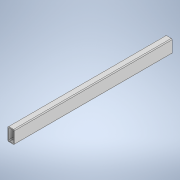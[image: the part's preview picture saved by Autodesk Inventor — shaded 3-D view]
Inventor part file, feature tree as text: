
AUTODESK INVENTOR PART (.ipt)
format: ipt  version: 2020 (Build 240168000, 168)  size: 124,416 bytes
history: native  units: in
note: dims shown in document units (in); Inventor stores cm internally (conversion verified against a paired STEP export)
features: extrude x1, sketch x1
ambient origin geometry x8: Origin, YZ Plane, XZ Plane, XY Plane, X Axis, Y Axis, Z Axis, Center Point
bodies: Solid1 (feature_tree)
feature tree (2):
  extrude  "Extrusion1"  Depth=1.0in
  sketch  "Sketch1"  dims[d0=2.0in d1=1.0in d2=0.125in d3=0.125in d4=0.125in d5=0.125in d6=0.125in d7=0.125in d8=0.125in d9=0.125in d10=0.125in d11=24.0in d12=0.0in]
